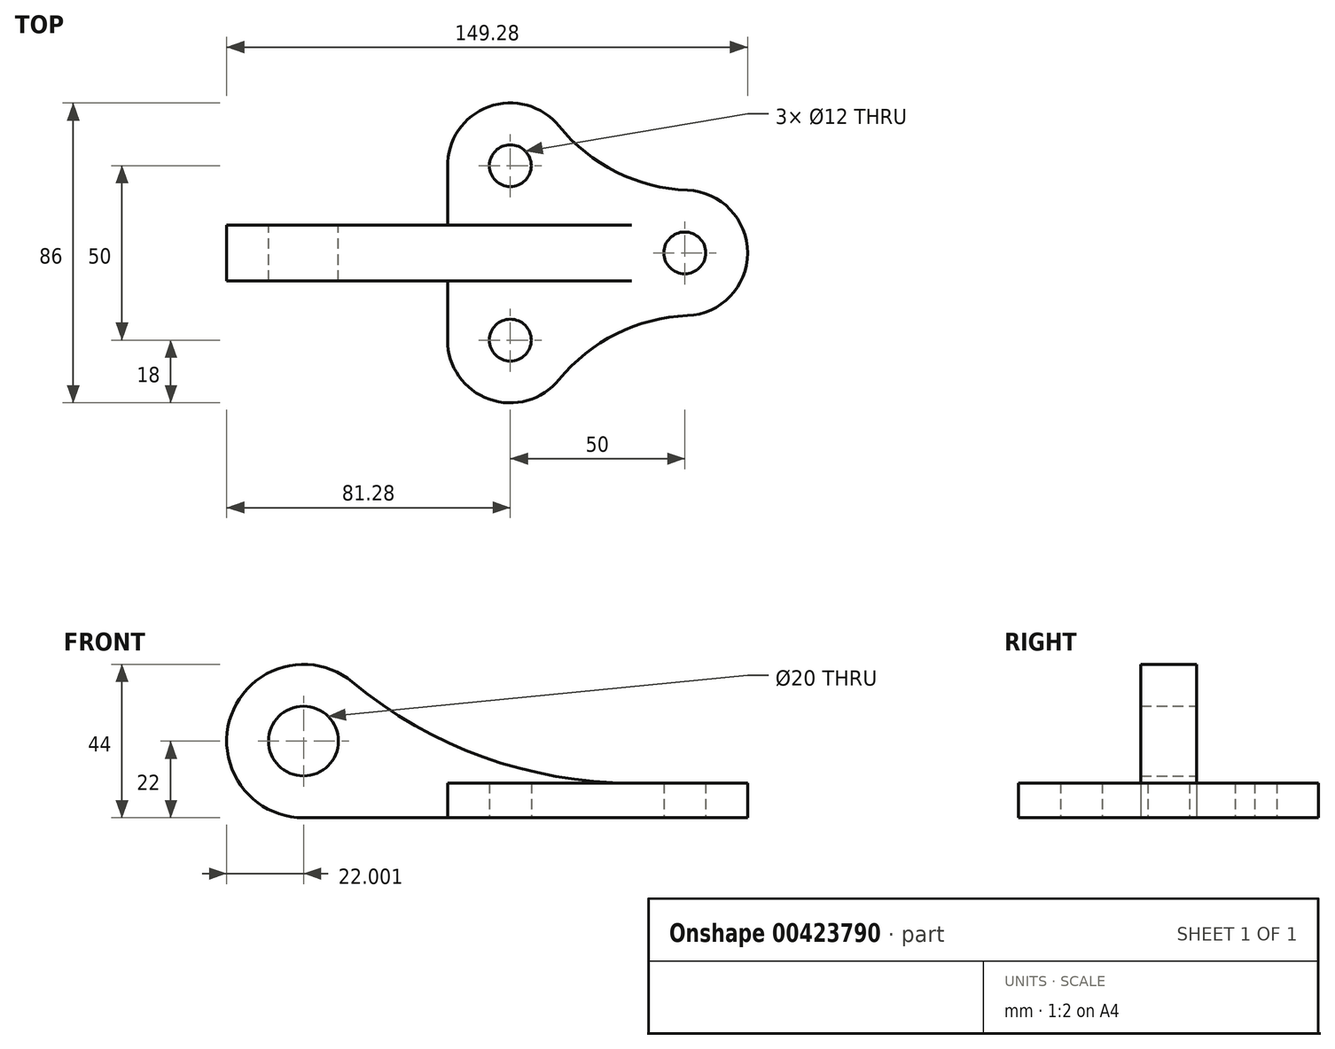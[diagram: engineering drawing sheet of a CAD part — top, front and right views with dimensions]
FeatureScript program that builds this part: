
annotation { "Feature Type Name" : "Feature", "Feature Type Description" : "" }
export const myFeature = defineFeature(function(context is Context, id is Id, definition is map)
    precondition{}
    {
        {
            var Q0;
            Q0=qCreatedBy(makeId("Top.planeOp"),FACE);
            var sketch = newSketch(context, id + "F0", { "sketchPlane" : qUnion([Q0])});
            skCircle(sketch, "E0", {"center": v(-50, 25) * mm, "radius": 18 * mm});
            skCircle(sketch, "E1", {"center": v(-50, -25) * mm, "radius": 18 * mm});
            skCircle(sketch, "E2", {"center": v(0, 0) * mm, "radius": 18 * mm});
            skCircle(sketch, "E3", {"center": v(-50, 25) * mm, "radius": 6 * mm});
            skCircle(sketch, "E4", {"center": v(-50, -25) * mm, "radius": 6 * mm});
            skCircle(sketch, "E5", {"center": v(0, 0) * mm, "radius": 6 * mm});
            skArc(sketch, "E6", {"start": v(0.72, -17.99) * mm, "mid": v(-19.64, -23.22) * mm, "end": v(-36.04, -36.37) * mm});
            skArc(sketch, "E7", {"start": v(-36.04, 36.37) * mm, "mid": v(-19.64, 23.22) * mm, "end": v(0.72, 17.99) * mm});
            skLineSegment(sketch, "E8", {"start": v(-68, 25.37) * mm, "end": v(-68, -25) * mm});
            skSolve(sketch);
        }
        {
            var Q0;
            Q0 = qSketchRegion(id + "F0", true);
            extrude(context, id + "F1", {"entities" : qUnion([Q0]), "depth" : 10 * mm});
        }
        {
            var Q0;
            Q0=qCreatedBy(makeId("Front.planeOp"),FACE);
            var sketch = newSketch(context, id + "F2", { "sketchPlane" : qUnion([Q0])});
            skCircle(sketch, "E9", {"center": v(-109.28, 22) * mm, "radius": 22 * mm});
            skLineSegment(sketch, "E10", {"start": v(0, 0) * mm, "end": v(-109.32, 0) * mm});
            skArc(sketch, "E11", {"start": v(-95.2, 38.91) * mm, "mid": v(-57.77, 17.45) * mm, "end": v(-15.26, 10) * mm});
            skLineSegment(sketch, "E12.0", {"start": v(0.72, 10) * mm, "end": v(-36.04, 10) * mm});
            skLineSegment(sketch, "E13", {"start": v(-15.26, 10) * mm, "end": v(-15.26, 0) * mm});
            skCircle(sketch, "E14", {"center": v(-109.28, 22) * mm, "radius": 10 * mm});
            skSolve(sketch);
        }
        {
            var Q0;
            Q0 = qSketchRegion(id + "F2", true);
            extrude(context, id + "F3", {"entities" : qUnion([Q0]), "operationType" : NewBodyOperationType.ADD, "endBound" : BoundingType.SYMMETRIC, "depth" : 16 * mm});
        }
    });
